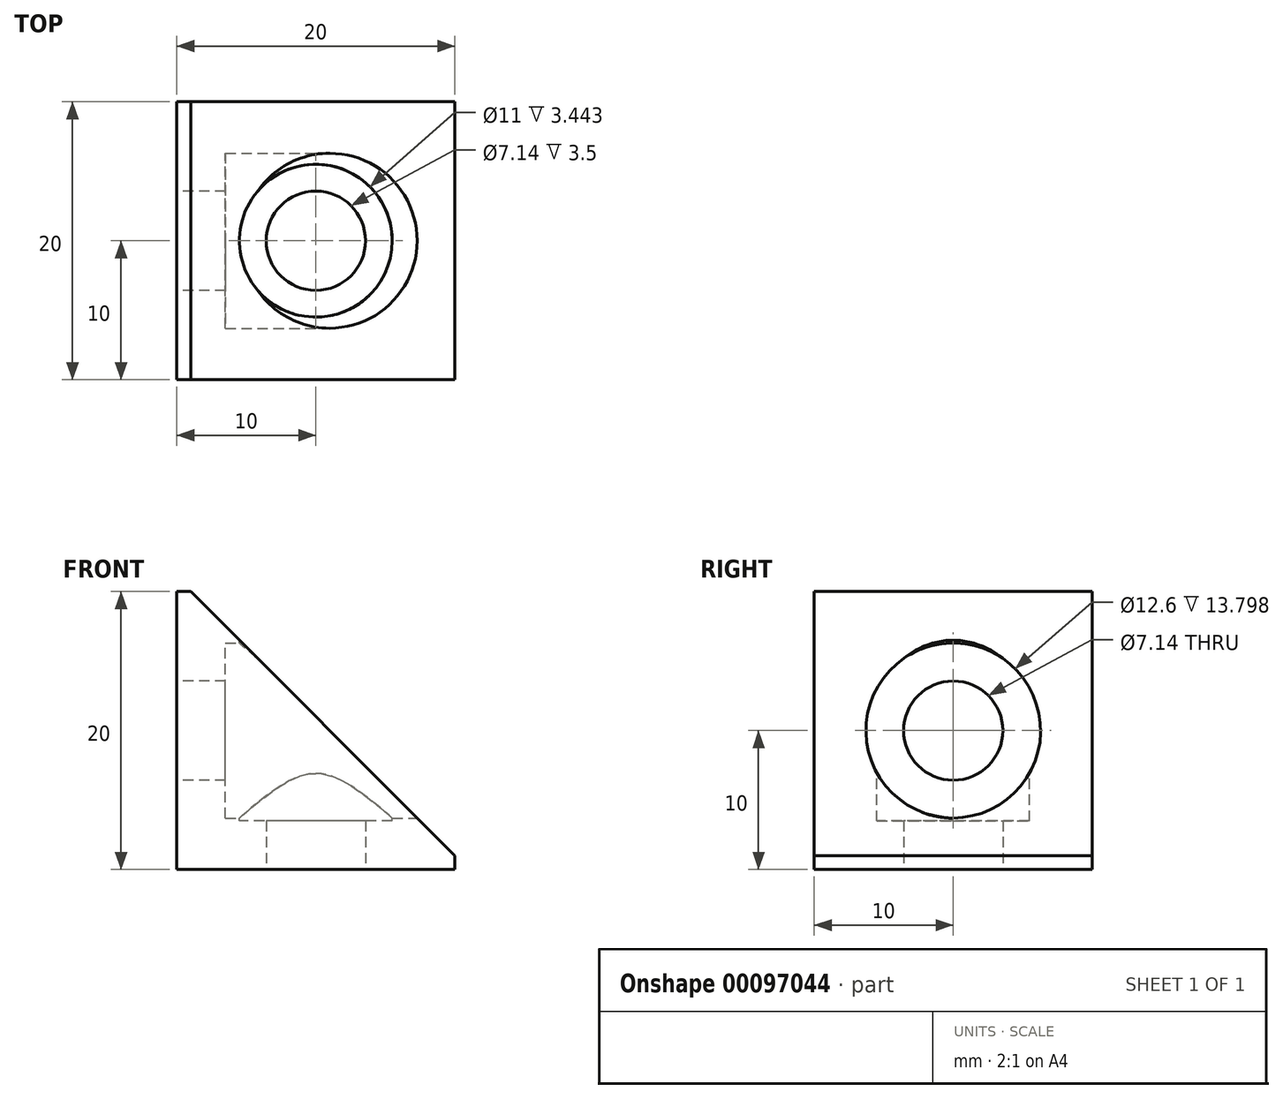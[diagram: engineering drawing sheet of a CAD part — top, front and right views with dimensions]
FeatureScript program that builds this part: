
annotation { "Feature Type Name" : "Feature", "Feature Type Description" : "" }
export const myFeature = defineFeature(function(context is Context, id is Id, definition is map)
    precondition{}
    {
        {
            var Q0;
            Q0=qCreatedBy(makeId("Top.planeOp"),FACE);
            var sketch = newSketch(context, id + "F0", { "sketchPlane" : qUnion([Q0])});
            skLineSegment(sketch, "E0.rect.bottom", {"start": v(10, 10) * mm, "end": v(-10, 10) * mm});
            skLineSegment(sketch, "E0.rect.top", {"start": v(10, -10) * mm, "end": v(-10, -10) * mm});
            skLineSegment(sketch, "E0.rect.left", {"start": v(10, 10) * mm, "end": v(10, -10) * mm});
            skLineSegment(sketch, "E0.rect.right", {"start": v(-10, 10) * mm, "end": v(-10, -10) * mm});
            skPoint(sketch, "E0.rect.middle", {"position": v(0, 0) * mm});
            skSolve(sketch);
        }
        {
            var Q0;
            Q0=qSketchRegion(id+"F0",true);
            extrude(context, id + "F1", {"entities" : qUnion([Q0]), "depth" : 20 * mm});
        }
        {
            var Q0;
            Q0=makeQuery(id+"F1.opExtrude","SWEPT_FACE",FACE,{"disambiguationData":[OSD([sQuery(id+"F0.wireOp",EDGE,"E0.rect.left")])]});
            var sketch = newSketch(context, id + "F2", { "sketchPlane" : qUnion([Q0])});
            skLineSegment(sketch, "E1", {"start": v(-10, 20) * mm, "end": v(10, 0) * mm, "construction": true});
            skLineSegment(sketch, "E2", {"start": v(10, 20) * mm, "end": v(-10, 0) * mm, "construction": true});
            skCircle(sketch, "E3", {"center": v(0, 10) * mm, "radius": 6.3 * mm});
            skSolve(sketch);
        }
        {
            var Q0;
            Q0=qSketchRegion(id+"F2",true);
            extrude(context, id + "F3", {"entities" : qUnion([Q0]), "operationType" : NewBodyOperationType.REMOVE, "oppositeDirection" : true, "depth" : 16.5 * mm});
        }
        {
            var Q0;
            Q0=makeQuery(id+"F1.opExtrude","CAP_FACE",FACE,{"disambiguationData":[OSD([sQuery(id+"F0.wireOp",EDGE,"E0.rect.bottom"),sQuery(id+"F0.wireOp",EDGE,"E0.rect.top"),sQuery(id+"F0.wireOp",EDGE,"E0.rect.left"),sQuery(id+"F0.wireOp",EDGE,"E0.rect.right")])],"isStart":false});
            var sketch = newSketch(context, id + "F4", { "sketchPlane" : qUnion([Q0])});
            skCircle(sketch, "E4", {"center": v(0, 0) * mm, "radius": 5.5 * mm});
            skSolve(sketch);
        }
        {
            var Q0;
            Q0=qSketchRegion(id+"F4",true);
            extrude(context, id + "F5", {"entities" : qUnion([Q0]), "operationType" : NewBodyOperationType.REMOVE, "oppositeDirection" : true, "depth" : 16.5 * mm});
        }
        {
            var Q0;
            Q0=makeQuery(id+"F1.opExtrude","CAP_FACE",FACE,{"disambiguationData":[OSD([sQuery(id+"F0.wireOp",EDGE,"E0.rect.bottom"),sQuery(id+"F0.wireOp",EDGE,"E0.rect.top"),sQuery(id+"F0.wireOp",EDGE,"E0.rect.left"),sQuery(id+"F0.wireOp",EDGE,"E0.rect.right")])],"isStart":true});
            var sketch = newSketch(context, id + "F6", { "sketchPlane" : qUnion([Q0])});
            skCircle(sketch, "E5", {"center": v(0, 0) * mm, "radius": 3.57 * mm});
            skSolve(sketch);
        }
        {
            var Q0;
            Q0=qSketchRegion(id+"F6",true);
            extrude(context, id + "F7", {"entities" : qUnion([Q0]), "operationType" : NewBodyOperationType.REMOVE, "endBound" : BoundingType.THROUGH_ALL, "oppositeDirection" : true, "depth" : 25 * mm});
        }
        {
            var Q0;
            Q0=makeQuery(id+"F1.opExtrude","SWEPT_FACE",FACE,{"disambiguationData":[OSD([sQuery(id+"F0.wireOp",EDGE,"E0.rect.right")])]});
            var sketch = newSketch(context, id + "F8", { "sketchPlane" : qUnion([Q0])});
            skLineSegment(sketch, "E6", {"start": v(-10, 20) * mm, "end": v(10, 0) * mm, "construction": true});
            skCircle(sketch, "E7", {"center": v(0, 10) * mm, "radius": 3.57 * mm});
            skSolve(sketch);
        }
        {
            var Q0;
            Q0=qSketchRegion(id+"F8",true);
            extrude(context, id + "F9", {"entities" : qUnion([Q0]), "operationType" : NewBodyOperationType.REMOVE, "endBound" : BoundingType.THROUGH_ALL, "oppositeDirection" : true, "depth" : 25 * mm});
        }
        {
            var Q0;
            Q0=makeQuery(id+"F1.opExtrude","SWEPT_FACE",FACE,{"disambiguationData":[OSD([sQuery(id+"F0.wireOp",EDGE,"E0.rect.bottom")])]});
            var sketch = newSketch(context, id + "F10", { "sketchPlane" : qUnion([Q0])});
            skLineSegment(sketch, "E8", {"start": v(-10, 20) * mm, "end": v(-10, 1) * mm});
            skLineSegment(sketch, "E9", {"start": v(-10, 1) * mm, "end": v(9, 20) * mm});
            skLineSegment(sketch, "E10", {"start": v(9, 20) * mm, "end": v(-10, 20) * mm});
            skSolve(sketch);
        }
        {
            var Q0;
            Q0=qSketchRegion(id+"F10",true);
            extrude(context, id + "F11", {"entities" : qUnion([Q0]), "operationType" : NewBodyOperationType.REMOVE, "endBound" : BoundingType.THROUGH_ALL, "oppositeDirection" : true, "depth" : 25 * mm});
        }
    });
